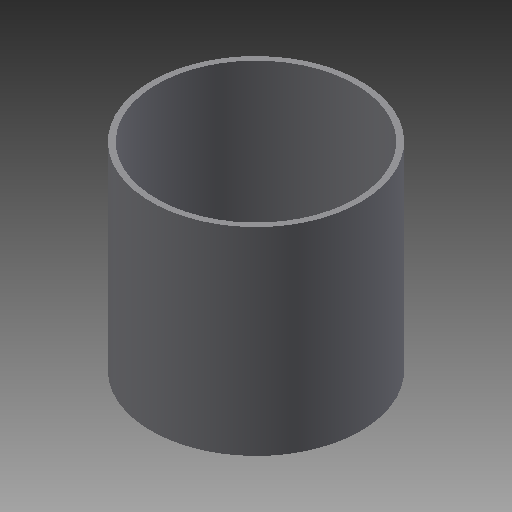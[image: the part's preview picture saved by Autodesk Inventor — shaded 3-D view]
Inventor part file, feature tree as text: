
AUTODESK INVENTOR PART (.ipt)
format: ipt  version: 2019.4 (Build 234330000, 330)  size: 126,464 bytes
history: native  units: in
note: dims shown in document units (in); Inventor stores cm internally (conversion verified against a paired STEP export)
features: other x84, revolve x1, sketch x1
ambient origin geometry x8: Origin, YZ Plane, XZ Plane, XY Plane, X Axis, Y Axis, Z Axis, Center Point
bodies: Solid1 (feature_tree)
feature tree (86):
  revolve  "Revolution1"  [1 undecoded]
  other  "rod_to_part_XY"
  other  "rod_to_part_YZ"
  other  "rod_to_part_ZX"
  other  "rod_to_part_X"
  other  "rod_to_part_Y"
  other  "rod_to_part_Z"
  other  "rod_to_part_Center"
  other  "to_road_XY"
  other  "to_road_YZ"
  other  "to_road_ZX"
  other  "to_road_X"
  other  "to_road_Y"
  other  "to_road_Z"
  other  "to_road_Center"
  other  "track1_XY"
  other  "track1_YZ"
  other  "track1_ZX"
  other  "track1_X"
  other  "track1_Y"
  other  "track1_Z"
  other  "track1_Center"
  other  "track1_u_XY"
  other  "track1_u_YZ"
  other  "track1_u_ZX"
  other  "track1_u_X"
  other  "track1_u_Y"
  other  "track1_u_Z"
  other  "track1_u_Center"
  other  "track2_XY"
  other  "track2_YZ"
  other  "track2_ZX"
  other  "track2_X"
  other  "track2_Y"
  other  "track2_Z"
  other  "track2_Center"
  other  "track2_u_XY"
  other  "track2_u_YZ"
  other  "track2_u_ZX"
  other  "track2_u_X"
  other  "track2_u_Y"
  other  "track2_u_Z"
  other  "track2_u_Center"
  other  "track3_XY"
  other  "track3_YZ"
  other  "track3_ZX"
  other  "track3_X"
  other  "track3_Y"
  other  "track3_Z"
  other  "track3_Center"
  other  "track3_u_XY"
  other  "track3_u_YZ"
  other  "track3_u_ZX"
  other  "track3_u_X"
  other  "track3_u_Y"
  other  "track3_u_Z"
  other  "track3_u_Center"
  other  "track4_XY"
  other  "track4_YZ"
  other  "track4_ZX"
  other  "track4_X"
  other  "track4_Y"
  other  "track4_Z"
  other  "track4_Center"
  other  "track4_u_XY"
  other  "track4_u_YZ"
  other  "track4_u_ZX"
  other  "track4_u_X"
  other  "track4_u_Y"
  other  "track4_u_Z"
  other  "track4_u_Center"
  other  "tube_rear_XY"
  other  "tube_rear_YZ"
  other  "tube_rear_ZX"
  other  "tube_rear_X"
  other  "tube_rear_Y"
  other  "tube_rear_Z"
  other  "tube_rear_Center"
  other  "tube_rod_guide_XY"
  other  "tube_rod_guide_YZ"
  other  "tube_rod_guide_ZX"
  other  "tube_rod_guide_X"
  other  "tube_rod_guide_Y"
  other  "tube_rod_guide_Z"
  other  "tube_rod_guide_Center"
  sketch  "Sketch_4"  dims[d0=360.0deg d1=0.0in d2=0.0in]
note: 1 required parameter value undecoded (feature->parameter linkage not recoverable at this tier; creation-order binding heuristic only, values carry confidence <= 0.55)
